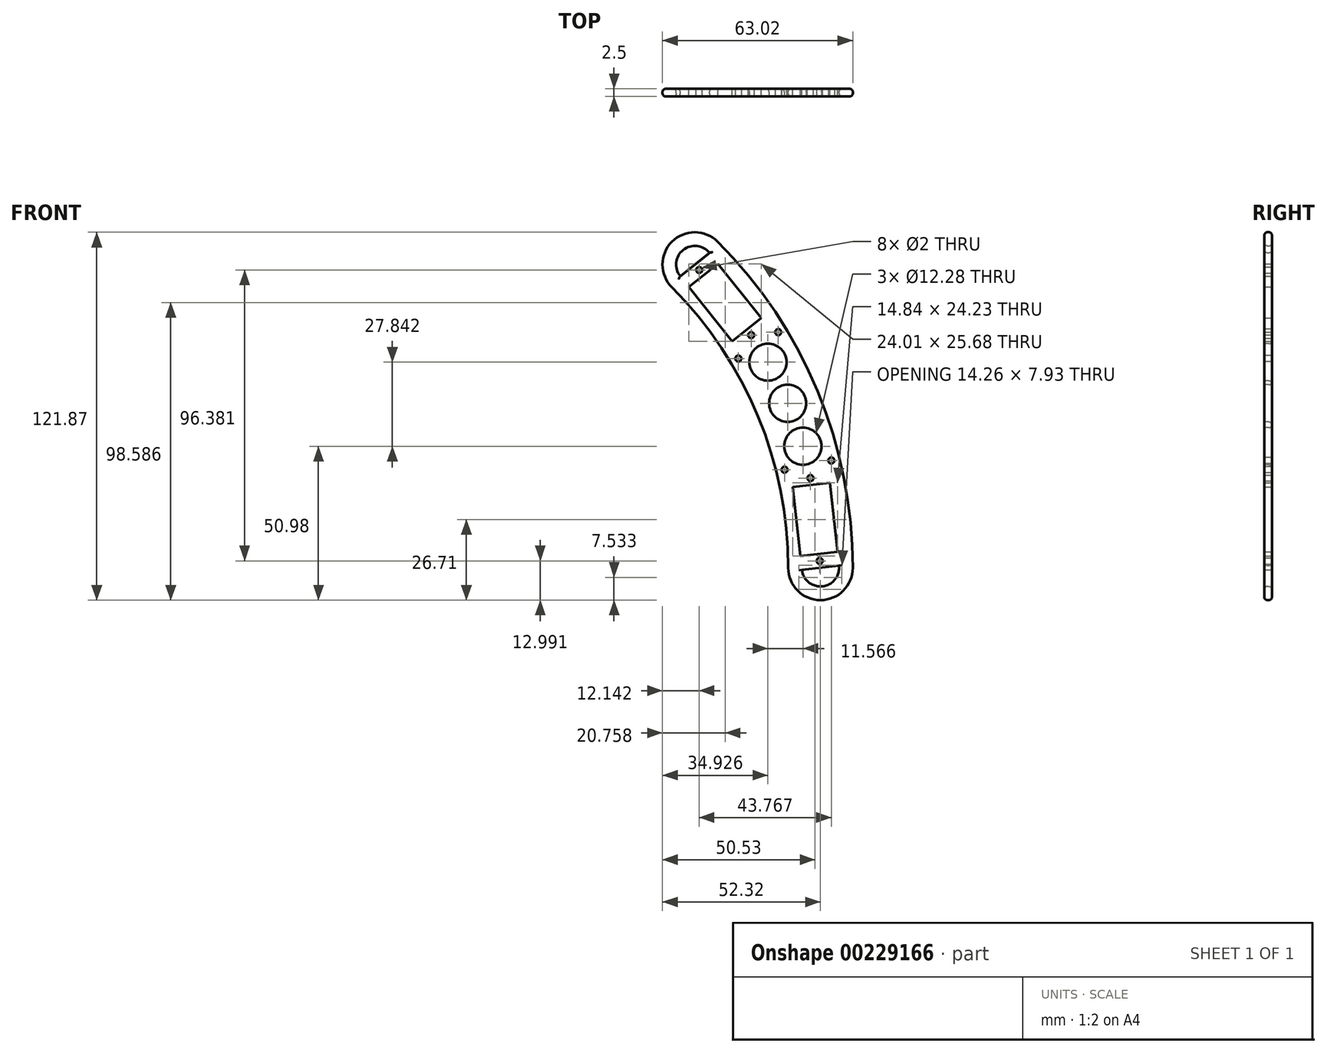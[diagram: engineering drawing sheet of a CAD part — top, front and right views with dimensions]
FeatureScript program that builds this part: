
annotation { "Feature Type Name" : "Feature", "Feature Type Description" : "" }
export const myFeature = defineFeature(function(context is Context, id is Id, definition is map)
    precondition{}
    {
        {
            var Q0;
            Q0=qCreatedBy(makeId("Front.planeOp"),FACE);
            var sketch = newSketch(context, id + "F0", { "sketchPlane" : qUnion([Q0])});
            skCircle(sketch, "E0", {"center": v(0, 0) * mm, "radius": 152.8 * mm});
            skCircle(sketch, "E1", {"center": v(0, 0) * mm, "radius": 131.4 * mm});
            skLineSegment(sketch, "E2", {"start": v(0, 0) * mm, "end": v(152.8, 0) * mm, "construction": true});
            skLineSegment(sketch, "E3", {"start": v(0, 0) * mm, "end": v(108.04, 108.04) * mm, "construction": true});
            skPoint(sketch, "E4", {"position": v(92.9, 92.9) * mm});
            skPoint(sketch, "E5", {"position": v(108.04, 108.04) * mm});
            skPoint(sketch, "E6", {"position": v(131.4, 0) * mm});
            skPoint(sketch, "E7", {"position": v(152.8, 0) * mm});
            skCircle(sketch, "E8", {"center": v(100.47, 100.47) * mm, "radius": 10.7 * mm});
            skCircle(sketch, "E9", {"center": v(142.1, 0) * mm, "radius": 10.7 * mm});
            skLineSegment(sketch, "E10", {"start": v(100.47, 100.47) * mm, "end": v(105.3, 104.33) * mm});
            skLineSegment(sketch, "E11", {"start": v(100.47, 100.47) * mm, "end": v(95.64, 96.62) * mm});
            skLineSegment(sketch, "E12", {"start": v(120.53, 75.25) * mm, "end": v(125.41, 79.16) * mm});
            skLineSegment(sketch, "E13", {"start": v(120.53, 75.25) * mm, "end": v(115.75, 71.44) * mm});
            skLineSegment(sketch, "E14", {"start": v(105.3, 104.33) * mm, "end": v(125.41, 79.16) * mm});
            skLineSegment(sketch, "E15", {"start": v(95.64, 96.62) * mm, "end": v(115.75, 71.44) * mm});
            skLineSegment(sketch, "E16", {"start": v(112.88, 75.04) * mm, "end": v(122.53, 82.76) * mm});
            skLineSegment(sketch, "E17", {"start": v(98.52, 93.01) * mm, "end": v(108.18, 100.73) * mm});
            skCircle(sketch, "E18", {"center": v(0, 0) * mm, "radius": 148.23 * mm, "construction": true});
            skCircle(sketch, "E19", {"center": v(0, 0) * mm, "radius": 135.95 * mm, "construction": true});
            skCircle(sketch, "E20", {"center": v(141.83, 2.3) * mm, "radius": 1 * mm});
            skLineSegment(sketch, "E21", {"start": v(122.53, 82.76) * mm, "end": v(115.75, 71.44) * mm, "construction": true});
            skLineSegment(sketch, "E22", {"start": v(112.88, 75.04) * mm, "end": v(125.41, 79.16) * mm, "construction": true});
            skCircle(sketch, "E23", {"center": v(101.91, 98.67) * mm, "radius": 1 * mm});
            skCircle(sketch, "E24", {"center": v(119.14, 77.1) * mm, "radius": 1 * mm});
            skCircle(sketch, "E25", {"center": v(107.2, 92.04) * mm, "radius": 6.18 * mm});
            skCircle(sketch, "E26", {"center": v(100.47, 100.47) * mm, "radius": 6.18 * mm});
            skCircle(sketch, "E27", {"center": v(142.1, 0) * mm, "radius": 6.17 * mm});
            skLineSegment(sketch, "E28", {"start": v(95.64, 96.62) * mm, "end": v(108.18, 100.73) * mm, "construction": true});
            skLineSegment(sketch, "E29", {"start": v(105.3, 104.33) * mm, "end": v(98.52, 93.01) * mm, "construction": true});
            skPoint(sketch, "E30", {"position": v(138.77, 29.73) * mm});
            skLineSegment(sketch, "E31", {"start": v(135.95, -0.69) * mm, "end": v(148.23, 0.69) * mm});
            skLineSegment(sketch, "E32", {"start": v(148.23, 0.69) * mm, "end": v(144.65, 32.7) * mm});
            skLineSegment(sketch, "E33", {"start": v(144.65, 32.7) * mm, "end": v(132.37, 31.33) * mm});
            skLineSegment(sketch, "E34", {"start": v(132.37, 31.33) * mm, "end": v(135.95, -0.69) * mm});
            skLineSegment(sketch, "E35", {"start": v(132.88, 26.75) * mm, "end": v(145.16, 28.13) * mm});
            skLineSegment(sketch, "E36", {"start": v(147.72, 5.27) * mm, "end": v(135.44, 3.9) * mm});
            skLineSegment(sketch, "E37", {"start": v(145.16, 28.13) * mm, "end": v(132.37, 31.33) * mm, "construction": true});
            skLineSegment(sketch, "E38", {"start": v(132.88, 26.75) * mm, "end": v(144.65, 32.7) * mm, "construction": true});
            skCircle(sketch, "E39", {"center": v(138.77, 29.73) * mm, "radius": 1 * mm});
            skLineSegment(sketch, "E40", {"start": v(147.72, 5.27) * mm, "end": v(135.95, -0.69) * mm, "construction": true});
            skLineSegment(sketch, "E41", {"start": v(148.23, 0.69) * mm, "end": v(135.44, 3.9) * mm, "construction": true});
            skCircle(sketch, "E42", {"center": v(140.9, 10.72) * mm, "radius": 6.18 * mm});
            skPoint(sketch, "E43", {"position": v(141.58, 4.58) * mm});
            skSolve(sketch);
        }
        {
            var Q0;
            {var subQ16=sQuery(id+"F0.wireOp",EDGE,"E13");Q0=makeQuery(id+"F0.imprint","IMPRINT",FACE,{"disambiguationData":[TD([[makeQuery(id+"F0.imprint","IMPRINT",EDGE,{"derivedFrom":subQ16}),1.0]])]});}
            var Q1;
            {var subQ14=sQuery(id+"F0.wireOp",EDGE,"E12");Q1=makeQuery(id+"F0.imprint","IMPRINT",FACE,{"disambiguationData":[TD([[makeQuery(id+"F0.imprint","IMPRINT",EDGE,{"derivedFrom":subQ14}),-1.0]])]});}
            var Q2;
            {var subQ3=sQuery(id+"F0.wireOp",EDGE,"oQQra7B9-EMDj-B2YQ-GpEd-beqhVWcHA2Qh");var subQ5=sQuery(id+"F0.wireOp",EDGE,"L7Lvz5JJ-y7Gk-G37b-dp0L-1B2kxOyyqlEU");var subQ9=makeQuery(id+"F0.imprint","INTERSECT",VERTEX,{"derivedFrom":[subQ3,subQ5]});Q2=makeQuery(id+"F0.imprint","IMPRINT",FACE,{"disambiguationData":[TD([[makeQuery(id+"F0.imprint","IMPRINT",EDGE,{"disambiguationData":[TD([[subQ9,-1.0]])],"derivedFrom":subQ3}),-1.0]])]});}
            var Q3;
            {var subQ3=sQuery(id+"F0.wireOp",EDGE,"oQQra7B9-EMDj-B2YQ-GpEd-beqhVWcHA2Qh");var subQ5=sQuery(id+"F0.wireOp",EDGE,"L7Lvz5JJ-y7Gk-G37b-dp0L-1B2kxOyyqlEU");var subQ9=makeQuery(id+"F0.imprint","INTERSECT",VERTEX,{"derivedFrom":[subQ3,subQ5]});Q3=makeQuery(id+"F0.imprint","IMPRINT",FACE,{"disambiguationData":[TD([[makeQuery(id+"F0.imprint","IMPRINT",EDGE,{"disambiguationData":[TD([[subQ9,-1.0]])],"derivedFrom":subQ3}),1.0]])]});}
            var Q4;
            {var subQ5=sQuery(id+"F0.wireOp",EDGE,"E9");var subQ8=makeQuery(id+"F0.imprint","INTERSECT",VERTEX,{"derivedFrom":[sQuery(id+"F0.wireOp",EDGE,"E1"),subQ5]});Q4=makeQuery(id+"F0.imprint","IMPRINT",FACE,{"disambiguationData":[TD([[makeQuery(id+"F0.imprint","IMPRINT",EDGE,{"disambiguationData":[TD([[subQ8,1.0]])],"derivedFrom":subQ5}),1.0]])]});}
            var Q5;
            {var subQ1=sQuery(id+"F0.wireOp",EDGE,"E9");var subQ5=makeQuery(id+"F0.imprint","INTERSECT",VERTEX,{"derivedFrom":[sQuery(id+"F0.wireOp",EDGE,"E0"),subQ1]});Q5=makeQuery(id+"F0.imprint","IMPRINT",FACE,{"disambiguationData":[TD([[makeQuery(id+"F0.imprint","IMPRINT",EDGE,{"disambiguationData":[TD([[subQ5,-1.0]])],"derivedFrom":subQ1}),1.0]])]});}
            var Q6;
            {var subQ1=sQuery(id+"F0.wireOp",EDGE,"pP7btSXe-vAWK-Rghq-c9eo-ooBtqokrkxCU");var subQ3=sQuery(id+"F0.wireOp",EDGE,"S4FxY1pI-YUIs-ADxV-D3kO-PCehrNdTsqgw");var subQ4=makeQuery(id+"F0.imprint","INTERSECT",VERTEX,{"derivedFrom":[subQ1,subQ3]});Q6=makeQuery(id+"F0.imprint","IMPRINT",FACE,{"disambiguationData":[TD([[makeQuery(id+"F0.imprint","IMPRINT",EDGE,{"disambiguationData":[TD([[subQ4,-1.0]])],"derivedFrom":subQ3}),-1.0]])]});}
            var Q7;
            {var subQ1=sQuery(id+"F0.wireOp",EDGE,"dObUoOk6-H3Xu-9Blf-IN91-eoC98K4MviYi");var subQ3=sQuery(id+"F0.wireOp",EDGE,"S4FxY1pI-YUIs-ADxV-D3kO-PCehrNdTsqgw");var subQ4=makeQuery(id+"F0.imprint","INTERSECT",VERTEX,{"derivedFrom":[subQ1,subQ3]});Q7=makeQuery(id+"F0.imprint","IMPRINT",FACE,{"disambiguationData":[TD([[makeQuery(id+"F0.imprint","IMPRINT",EDGE,{"disambiguationData":[TD([[subQ4,1.0]])],"derivedFrom":subQ3}),-1.0]])]});}
            var Q8;
            {var subQ4=sQuery(id+"F0.wireOp",EDGE,"E8");var subQ5=makeQuery(id+"F0.imprint","INTERSECT",VERTEX,{"derivedFrom":[sQuery(id+"F0.wireOp",EDGE,"E0"),subQ4]});Q8=makeQuery(id+"F0.imprint","IMPRINT",FACE,{"disambiguationData":[TD([[makeQuery(id+"F0.imprint","IMPRINT",EDGE,{"disambiguationData":[TD([[subQ5,-1.0]])],"derivedFrom":subQ4}),1.0]])]});}
            var Q9;
            {var subQ5=sQuery(id+"F0.wireOp",EDGE,"E8");var subQ9=makeQuery(id+"F0.imprint","INTERSECT",VERTEX,{"derivedFrom":[sQuery(id+"F0.wireOp",EDGE,"E1"),subQ5]});Q9=makeQuery(id+"F0.imprint","IMPRINT",FACE,{"disambiguationData":[TD([[makeQuery(id+"F0.imprint","IMPRINT",EDGE,{"disambiguationData":[TD([[subQ9,1.0]])],"derivedFrom":subQ5}),1.0]])]});}
            var Q10;
            {var subQ1=sQuery(id+"F0.wireOp",EDGE,"E15");var subQ3=sQuery(id+"F0.wireOp",EDGE,"E17");var subQ4=makeQuery(id+"F0.imprint","INTERSECT",VERTEX,{"derivedFrom":[subQ1,subQ3]});Q10=makeQuery(id+"F0.imprint","IMPRINT",FACE,{"disambiguationData":[TD([[makeQuery(id+"F0.imprint","IMPRINT",EDGE,{"disambiguationData":[TD([[subQ4,-1.0]])],"derivedFrom":subQ3}),1.0]])]});}
            var Q11;
            {var subQ4=sQuery(id+"F0.wireOp",EDGE,"E11");Q11=makeQuery(id+"F0.imprint","IMPRINT",FACE,{"disambiguationData":[TD([[makeQuery(id+"F0.imprint","IMPRINT",EDGE,{"derivedFrom":subQ4}),1.0]])]});}
            var Q12;
            {var subQ0=sQuery(id+"F0.wireOp",EDGE,"E10");Q12=makeQuery(id+"F0.imprint","IMPRINT",FACE,{"disambiguationData":[TD([[makeQuery(id+"F0.imprint","IMPRINT",EDGE,{"derivedFrom":subQ0}),-1.0]])]});}
            var Q13;
            {var subQ1=sQuery(id+"F0.wireOp",EDGE,"E14");var subQ3=sQuery(id+"F0.wireOp",EDGE,"E17");var subQ4=makeQuery(id+"F0.imprint","INTERSECT",VERTEX,{"derivedFrom":[subQ1,subQ3]});Q13=makeQuery(id+"F0.imprint","IMPRINT",FACE,{"disambiguationData":[TD([[makeQuery(id+"F0.imprint","IMPRINT",EDGE,{"disambiguationData":[TD([[subQ4,1.0]])],"derivedFrom":subQ3}),1.0]])]});}
            var Q14;
            {var subQ1=sQuery(id+"F0.wireOp",EDGE,"E13");Q14=makeQuery(id+"F0.imprint","IMPRINT",FACE,{"disambiguationData":[TD([[makeQuery(id+"F0.imprint","IMPRINT",EDGE,{"derivedFrom":subQ1}),-1.0]])]});}
            var Q15;
            {var subQ1=sQuery(id+"F0.wireOp",EDGE,"E12");Q15=makeQuery(id+"F0.imprint","IMPRINT",FACE,{"disambiguationData":[TD([[makeQuery(id+"F0.imprint","IMPRINT",EDGE,{"derivedFrom":subQ1}),1.0]])]});}
            var Q16;
            {var subQ0=sQuery(id+"F0.wireOp",EDGE,"OI4elRIE-cDK8-WTxH-k70q-1QsIJyjjSFf5");Q16=makeQuery(id+"F0.imprint","IMPRINT",FACE,{"disambiguationData":[TD([[makeQuery(id+"F0.imprint","IMPRINT",EDGE,{"derivedFrom":subQ0}),-1.0]])]});}
            var Q17;
            {var subQ5=sQuery(id+"F0.wireOp",EDGE,"jRu6URXB-eb1m-GeLn-RnXG-8x56v3XeeYK7");Q17=makeQuery(id+"F0.imprint","IMPRINT",FACE,{"disambiguationData":[TD([[makeQuery(id+"F0.imprint","IMPRINT",EDGE,{"derivedFrom":subQ5}),1.0]])]});}
            var Q18;
            Q18=makeQuery(id+"F0.imprint","IMPRINT",FACE,{"disambiguationData":[TD([[makeQuery(id+"F0.imprint","IMPRINT",EDGE,{"derivedFrom":sQuery(id+"F0.wireOp",EDGE,"E20")}),-1.0]])]});
            var Q19;
            {var subQ0=sQuery(id+"F0.wireOp",EDGE,"E36");var subQ1=sQuery(id+"F0.wireOp",EDGE,"E27");var subQ2=makeQuery(id+"F0.imprint","INTERSECT",VERTEX,{"disambiguationData":[OD(1.0)],"derivedFrom":[subQ1,subQ0]});Q19=makeQuery(id+"F0.imprint","IMPRINT",FACE,{"disambiguationData":[TD([[makeQuery(id+"F0.imprint","IMPRINT",EDGE,{"disambiguationData":[TD([[subQ2,-1.0]])],"derivedFrom":subQ1}),-1.0]])]});}
            var Q20;
            {var subQ0=sQuery(id+"F0.wireOp",EDGE,"E36");var subQ1=sQuery(id+"F0.wireOp",EDGE,"E27");var subQ2=makeQuery(id+"F0.imprint","INTERSECT",VERTEX,{"disambiguationData":[OD(0.0)],"derivedFrom":[subQ1,subQ0]});Q20=makeQuery(id+"F0.imprint","IMPRINT",FACE,{"disambiguationData":[TD([[makeQuery(id+"F0.imprint","IMPRINT",EDGE,{"disambiguationData":[TD([[subQ2,1.0]])],"derivedFrom":subQ1}),-1.0]])]});}
            var Q21;
            {var subQ2=sQuery(id+"F0.wireOp",EDGE,"E33");Q21=makeQuery(id+"F0.imprint","IMPRINT",FACE,{"disambiguationData":[TD([[makeQuery(id+"F0.imprint","IMPRINT",EDGE,{"derivedFrom":subQ2}),1.0]])]});}
            extrude(context, id + "F1", {"entities" : qUnion([Q0, Q1, Q2, Q3, Q4, Q5, Q6, Q7, Q8, Q9, Q10, Q11, Q12, Q13, Q14, Q15, Q16, Q17, Q18, Q19, Q20, Q21]), "depth" : 2.5 * mm});
        }
        {
            var Q0;
            Q0=makeQuery(id+"F1.opExtrude","CAP_FACE",FACE,{"disambiguationData":[OSD([sQuery(id+"F0.wireOp",EDGE,"E0"),sQuery(id+"F0.wireOp",EDGE,"E1"),sQuery(id+"F0.wireOp",EDGE,"E8"),sQuery(id+"F0.wireOp",EDGE,"E9"),sQuery(id+"F0.wireOp",EDGE,"jRu6URXB-eb1m-GeLn-RnXG-8x56v3XeeYK7"),sQuery(id+"F0.wireOp",EDGE,"SvjzzxK2-7mAt-kCR1-GuG7-fGwirkntV4HA"),sQuery(id+"F0.wireOp",EDGE,"dObUoOk6-H3Xu-9Blf-IN91-eoC98K4MviYi"),sQuery(id+"F0.wireOp",EDGE,"pP7btSXe-vAWK-Rghq-c9eo-ooBtqokrkxCU"),sQuery(id+"F0.wireOp",EDGE,"E10"),sQuery(id+"F0.wireOp",EDGE,"E11"),sQuery(id+"F0.wireOp",EDGE,"E14"),sQuery(id+"F0.wireOp",EDGE,"E15"),sQuery(id+"F0.wireOp",EDGE,"S4FxY1pI-YUIs-ADxV-D3kO-PCehrNdTsqgw"),sQuery(id+"F0.wireOp",EDGE,"L7Lvz5JJ-y7Gk-G37b-dp0L-1B2kxOyyqlEU"),sQuery(id+"F0.wireOp",EDGE,"E16"),sQuery(id+"F0.wireOp",EDGE,"E17"),sQuery(id+"F0.wireOp",EDGE,"E20"),sQuery(id+"F0.wireOp",EDGE,"xssTYC09-HPZV-zy9G-g6WS-DKxBsCUwhTFc"),sQuery(id+"F0.wireOp",EDGE,"E23"),sQuery(id+"F0.wireOp",EDGE,"E24"),sQuery(id+"F0.wireOp",EDGE,"E26"),sQuery(id+"F0.wireOp",EDGE,"E27")])],"isStart":false});
            var sketch = newSketch(context, id + "F2", { "sketchPlane" : qUnion([Q0])});
            skCircle(sketch, "E44", {"center": v(136.26, 40.28) * mm, "radius": 6.14 * mm});
            skCircle(sketch, "E45", {"center": v(124.7, 68.12) * mm, "radius": 6.14 * mm});
            skCircle(sketch, "E46", {"center": v(131.22, 54.5) * mm, "radius": 6.14 * mm});
            skCircle(sketch, "E47", {"center": v(0, 0) * mm, "radius": 142.1 * mm, "construction": true});
            skLineSegment(sketch, "E48", {"start": v(0, 0) * mm, "end": v(118, 79.14) * mm, "construction": true});
            skLineSegment(sketch, "E49", {"start": v(0, 0) * mm, "end": v(139.35, 27.76) * mm, "construction": true});
            skLineSegment(sketch, "E50", {"start": v(0, 0) * mm, "end": v(136.26, 40.28) * mm, "construction": true});
            skLineSegment(sketch, "E51", {"start": v(0, 0) * mm, "end": v(131.22, 54.5) * mm, "construction": true});
            skLineSegment(sketch, "E52", {"start": v(0, 0) * mm, "end": v(124.7, 68.12) * mm, "construction": true});
            skCircle(sketch, "E53", {"center": v(0, 0) * mm, "radius": 152.8 * mm, "construction": true});
            skCircle(sketch, "E54", {"center": v(0, 0) * mm, "radius": 131.4 * mm, "construction": true});
            skCircle(sketch, "E55", {"center": v(0, 0) * mm, "radius": 135.95 * mm, "construction": true});
            skCircle(sketch, "E56", {"center": v(0, 0) * mm, "radius": 148.23 * mm, "construction": true});
            skLineSegment(sketch, "E57", {"start": v(112.88, 75.04) * mm, "end": v(119.3, 65.18) * mm, "construction": true});
            skLineSegment(sketch, "E58", {"start": v(119.3, 65.18) * mm, "end": v(118, 79.14) * mm, "construction": true});
            skLineSegment(sketch, "E59", {"start": v(118, 79.14) * mm, "end": v(130.08, 71.07) * mm, "construction": true});
            skLineSegment(sketch, "E60", {"start": v(130.08, 71.07) * mm, "end": v(122.53, 82.76) * mm, "construction": true});
            skLineSegment(sketch, "E61", {"start": v(122.53, 82.76) * mm, "end": v(118, 79.14) * mm});
            skLineSegment(sketch, "E62", {"start": v(112.88, 75.04) * mm, "end": v(118, 79.14) * mm});
            skLineSegment(sketch, "E63", {"start": v(126.3, 76.91) * mm, "end": v(130.43, 79.57) * mm, "construction": true});
            skCircle(sketch, "E64", {"center": v(128.1, 78.07) * mm, "radius": 1 * mm});
            skLineSegment(sketch, "E65", {"start": v(130.37, 38.54) * mm, "end": v(132.76, 27) * mm});
            skLineSegment(sketch, "E66", {"start": v(145.04, 28.42) * mm, "end": v(142.22, 41.78) * mm});
            skLineSegment(sketch, "E67", {"start": v(131.57, 32.77) * mm, "end": v(127.45, 31.92) * mm});
            skLineSegment(sketch, "E68", {"start": v(143.63, 35.1) * mm, "end": v(148.46, 36.12) * mm});
            skCircle(sketch, "E69", {"center": v(130.18, 32.48) * mm, "radius": 1 * mm});
            skCircle(sketch, "E70", {"center": v(145.68, 35.54) * mm, "radius": 1 * mm});
            skLineSegment(sketch, "E71", {"start": v(116.1, 70.11) * mm, "end": v(112.55, 67.8) * mm, "construction": true});
            skCircle(sketch, "E72", {"center": v(114.87, 69.32) * mm, "radius": 1 * mm});
            skSolve(sketch);
        }
        {
            var Q0;
            Q0=makeQuery(id+"F2.imprint","IMPRINT",FACE,{"disambiguationData":[TD([[makeQuery(id+"F2.imprint","IMPRINT",EDGE,{"derivedFrom":sQuery(id+"F2.wireOp",EDGE,"E45")}),1.0]])]});
            var Q1;
            Q1=makeQuery(id+"F2.imprint","IMPRINT",FACE,{"disambiguationData":[TD([[makeQuery(id+"F2.imprint","IMPRINT",EDGE,{"derivedFrom":sQuery(id+"F2.wireOp",EDGE,"E46")}),1.0]])]});
            var Q2;
            Q2=makeQuery(id+"F2.imprint","IMPRINT",FACE,{"disambiguationData":[TD([[makeQuery(id+"F2.imprint","IMPRINT",EDGE,{"derivedFrom":sQuery(id+"F2.wireOp",EDGE,"E44")}),1.0]])]});
            var Q3;
            {var subQ0=sQuery(id+"F2.wireOp",EDGE,"E60");var subQ1=sQuery(id+"F2.wireOp",EDGE,"E45");var subQ2=makeQuery(id+"F2.imprint","INTERSECT",VERTEX,{"derivedFrom":[subQ1,subQ0]});Q3=makeQuery(id+"F2.imprint","IMPRINT",FACE,{"disambiguationData":[TD([[makeQuery(id+"F2.imprint","IMPRINT",EDGE,{"disambiguationData":[TD([[subQ2,-1.0]])],"derivedFrom":subQ1}),1.0]])]});}
            var Q4;
            {var subQ0=sQuery(id+"F2.wireOp",EDGE,"E58");var subQ1=sQuery(id+"F2.wireOp",EDGE,"E45");var subQ3=makeQuery(id+"F2.imprint","INTERSECT",VERTEX,{"derivedFrom":[subQ1,subQ0]});Q4=makeQuery(id+"F2.imprint","IMPRINT",FACE,{"disambiguationData":[TD([[makeQuery(id+"F2.imprint","IMPRINT",EDGE,{"disambiguationData":[TD([[subQ3,-1.0]])],"derivedFrom":subQ1}),1.0]])]});}
            var Q5;
            Q5=makeQuery(id+"F2.imprint","IMPRINT",FACE,{"disambiguationData":[TD([[makeQuery(id+"F2.imprint","IMPRINT",EDGE,{"derivedFrom":sQuery(id+"F2.wireOp",EDGE,"6Q9i7ZKX-M5Zn-dDvE-S5ua-DKoOSJd4rO0q")}),1.0]])]});
            var Q6;
            Q6=makeQuery(id+"F2.imprint","IMPRINT",FACE,{"disambiguationData":[TD([[makeQuery(id+"F2.imprint","IMPRINT",EDGE,{"derivedFrom":sQuery(id+"F2.wireOp",EDGE,"E64")}),1.0]])]});
            var Q7;
            Q7=makeQuery(id+"F2.imprint","IMPRINT",FACE,{"disambiguationData":[TD([[makeQuery(id+"F2.imprint","IMPRINT",EDGE,{"derivedFrom":sQuery(id+"F2.wireOp",EDGE,"E72")}),1.0]])]});
            var Q8;
            {var subQ0=sQuery(id+"F2.wireOp",EDGE,"E70");var subQ1=sQuery(id+"F2.wireOp",EDGE,"E68");var subQ2=makeQuery(id+"F2.imprint","INTERSECT",VERTEX,{"disambiguationData":[OD(0.0)],"derivedFrom":[subQ1,subQ0]});Q8=makeQuery(id+"F2.imprint","IMPRINT",FACE,{"disambiguationData":[TD([[makeQuery(id+"F2.imprint","IMPRINT",EDGE,{"disambiguationData":[TD([[subQ2,-1.0]])],"derivedFrom":subQ1}),1.0]])]});}
            var Q9;
            {var subQ0=sQuery(id+"F2.wireOp",EDGE,"E70");var subQ1=sQuery(id+"F2.wireOp",EDGE,"E68");var subQ2=makeQuery(id+"F2.imprint","INTERSECT",VERTEX,{"disambiguationData":[OD(0.0)],"derivedFrom":[subQ1,subQ0]});Q9=makeQuery(id+"F2.imprint","IMPRINT",FACE,{"disambiguationData":[TD([[makeQuery(id+"F2.imprint","IMPRINT",EDGE,{"disambiguationData":[TD([[subQ2,-1.0]])],"derivedFrom":subQ1}),-1.0]])]});}
            var Q10;
            {var subQ0=sQuery(id+"F2.wireOp",EDGE,"E69");var subQ1=sQuery(id+"F2.wireOp",EDGE,"E67");var subQ2=makeQuery(id+"F2.imprint","INTERSECT",VERTEX,{"disambiguationData":[OD(0.0)],"derivedFrom":[subQ1,subQ0]});Q10=makeQuery(id+"F2.imprint","IMPRINT",FACE,{"disambiguationData":[TD([[makeQuery(id+"F2.imprint","IMPRINT",EDGE,{"disambiguationData":[TD([[subQ2,-1.0]])],"derivedFrom":subQ1}),1.0]])]});}
            var Q11;
            {var subQ0=sQuery(id+"F2.wireOp",EDGE,"E69");var subQ1=sQuery(id+"F2.wireOp",EDGE,"E67");var subQ2=makeQuery(id+"F2.imprint","INTERSECT",VERTEX,{"disambiguationData":[OD(0.0)],"derivedFrom":[subQ1,subQ0]});Q11=makeQuery(id+"F2.imprint","IMPRINT",FACE,{"disambiguationData":[TD([[makeQuery(id+"F2.imprint","IMPRINT",EDGE,{"disambiguationData":[TD([[subQ2,-1.0]])],"derivedFrom":subQ1}),-1.0]])]});}
            extrude(context, id + "F3", {"entities" : qUnion([Q0, Q1, Q2, Q3, Q4, Q5, Q6, Q7, Q8, Q9, Q10, Q11]), "operationType" : NewBodyOperationType.REMOVE, "oppositeDirection" : true, "depth" : 25 * mm});
        }
        {
            var Q0;
            Q0=makeQuery(id+"F1.opExtrude","CAP_EDGE",EDGE,{"disambiguationData":[OSD([sQuery(id+"F0.wireOp",EDGE,"E27")])],"isStart":true});
            var Q1;
            Q1=makeQuery(id+"F1.opExtrude","CAP_EDGE",EDGE,{"disambiguationData":[OSD([sQuery(id+"F0.wireOp",EDGE,"E27")])],"isStart":false});
            var Q2;
            Q2=makeQuery(id+"F1.opExtrude","CAP_EDGE",EDGE,{"disambiguationData":[OSD([sQuery(id+"F0.wireOp",EDGE,"E9")])],"isStart":true});
            var Q3;
            Q3=makeQuery(id+"F1.opExtrude","CAP_EDGE",EDGE,{"disambiguationData":[OSD([sQuery(id+"F0.wireOp",EDGE,"E0")])],"isStart":false});
            var Q4;
            Q4=makeQuery(id+"F1.opExtrude","CAP_EDGE",EDGE,{"disambiguationData":[OSD([sQuery(id+"F0.wireOp",EDGE,"E26")])],"isStart":false});
            var Q5;
            Q5=makeQuery(id+"F1.opExtrude","CAP_EDGE",EDGE,{"disambiguationData":[OSD([sQuery(id+"F0.wireOp",EDGE,"E26")])],"isStart":true});
            var Q6;
            Q6=makeQuery(id+"F3.boolean.opBoolean","COPY",EDGE,{"derivedFrom":makeQuery(id+"F3.opExtrude","CAP_EDGE",EDGE,{"disambiguationData":[OSD([sQuery(id+"F2.wireOp",EDGE,"E45")])],"isStart":true})});
            var Q7;
            Q7=makeQuery(id+"F3.boolean.opBoolean","COPY",EDGE,{"derivedFrom":makeQuery(id+"F3.opExtrude","CAP_EDGE",EDGE,{"disambiguationData":[OSD([sQuery(id+"F2.wireOp",EDGE,"E46")])],"isStart":true})});
            var Q8;
            Q8=makeQuery(id+"F3.boolean.opBoolean","COPY",EDGE,{"derivedFrom":makeQuery(id+"F3.opExtrude","CAP_EDGE",EDGE,{"disambiguationData":[OSD([sQuery(id+"F2.wireOp",EDGE,"E44")])],"isStart":true})});
            var Q9;
            Q9=makeQuery(id+"F3.boolean.opBoolean","INTERSECT",EDGE,{"derivedFrom":[makeQuery(id+"F1.opExtrude","CAP_FACE",FACE,{"disambiguationData":[OSD([sQuery(id+"F0.wireOp",EDGE,"E0"),sQuery(id+"F0.wireOp",EDGE,"E1"),sQuery(id+"F0.wireOp",EDGE,"E8"),sQuery(id+"F0.wireOp",EDGE,"E9"),sQuery(id+"F0.wireOp",EDGE,"jRu6URXB-eb1m-GeLn-RnXG-8x56v3XeeYK7"),sQuery(id+"F0.wireOp",EDGE,"SvjzzxK2-7mAt-kCR1-GuG7-fGwirkntV4HA"),sQuery(id+"F0.wireOp",EDGE,"dObUoOk6-H3Xu-9Blf-IN91-eoC98K4MviYi"),sQuery(id+"F0.wireOp",EDGE,"pP7btSXe-vAWK-Rghq-c9eo-ooBtqokrkxCU"),sQuery(id+"F0.wireOp",EDGE,"E10"),sQuery(id+"F0.wireOp",EDGE,"E11"),sQuery(id+"F0.wireOp",EDGE,"E14"),sQuery(id+"F0.wireOp",EDGE,"E15"),sQuery(id+"F0.wireOp",EDGE,"S4FxY1pI-YUIs-ADxV-D3kO-PCehrNdTsqgw"),sQuery(id+"F0.wireOp",EDGE,"L7Lvz5JJ-y7Gk-G37b-dp0L-1B2kxOyyqlEU"),sQuery(id+"F0.wireOp",EDGE,"E16"),sQuery(id+"F0.wireOp",EDGE,"E17"),sQuery(id+"F0.wireOp",EDGE,"E20"),sQuery(id+"F0.wireOp",EDGE,"xssTYC09-HPZV-zy9G-g6WS-DKxBsCUwhTFc"),sQuery(id+"F0.wireOp",EDGE,"E23"),sQuery(id+"F0.wireOp",EDGE,"E24"),sQuery(id+"F0.wireOp",EDGE,"E26"),sQuery(id+"F0.wireOp",EDGE,"E27")])],"isStart":true}),makeQuery(id+"F3.opExtrude","SWEPT_FACE",FACE,{"disambiguationData":[OSD([sQuery(id+"F2.wireOp",EDGE,"E45")])]})]});
            var Q10;
            Q10=makeQuery(id+"F3.boolean.opBoolean","INTERSECT",EDGE,{"derivedFrom":[makeQuery(id+"F1.opExtrude","CAP_FACE",FACE,{"disambiguationData":[OSD([sQuery(id+"F0.wireOp",EDGE,"E0"),sQuery(id+"F0.wireOp",EDGE,"E1"),sQuery(id+"F0.wireOp",EDGE,"E8"),sQuery(id+"F0.wireOp",EDGE,"E9"),sQuery(id+"F0.wireOp",EDGE,"jRu6URXB-eb1m-GeLn-RnXG-8x56v3XeeYK7"),sQuery(id+"F0.wireOp",EDGE,"SvjzzxK2-7mAt-kCR1-GuG7-fGwirkntV4HA"),sQuery(id+"F0.wireOp",EDGE,"dObUoOk6-H3Xu-9Blf-IN91-eoC98K4MviYi"),sQuery(id+"F0.wireOp",EDGE,"pP7btSXe-vAWK-Rghq-c9eo-ooBtqokrkxCU"),sQuery(id+"F0.wireOp",EDGE,"E10"),sQuery(id+"F0.wireOp",EDGE,"E11"),sQuery(id+"F0.wireOp",EDGE,"E14"),sQuery(id+"F0.wireOp",EDGE,"E15"),sQuery(id+"F0.wireOp",EDGE,"S4FxY1pI-YUIs-ADxV-D3kO-PCehrNdTsqgw"),sQuery(id+"F0.wireOp",EDGE,"L7Lvz5JJ-y7Gk-G37b-dp0L-1B2kxOyyqlEU"),sQuery(id+"F0.wireOp",EDGE,"E16"),sQuery(id+"F0.wireOp",EDGE,"E17"),sQuery(id+"F0.wireOp",EDGE,"E20"),sQuery(id+"F0.wireOp",EDGE,"xssTYC09-HPZV-zy9G-g6WS-DKxBsCUwhTFc"),sQuery(id+"F0.wireOp",EDGE,"E23"),sQuery(id+"F0.wireOp",EDGE,"E24"),sQuery(id+"F0.wireOp",EDGE,"E26"),sQuery(id+"F0.wireOp",EDGE,"E27")])],"isStart":true}),makeQuery(id+"F3.opExtrude","SWEPT_FACE",FACE,{"disambiguationData":[OSD([sQuery(id+"F2.wireOp",EDGE,"E46")])]})]});
            var Q11;
            Q11=makeQuery(id+"F3.boolean.opBoolean","INTERSECT",EDGE,{"derivedFrom":[makeQuery(id+"F1.opExtrude","CAP_FACE",FACE,{"disambiguationData":[OSD([sQuery(id+"F0.wireOp",EDGE,"E0"),sQuery(id+"F0.wireOp",EDGE,"E1"),sQuery(id+"F0.wireOp",EDGE,"E8"),sQuery(id+"F0.wireOp",EDGE,"E9"),sQuery(id+"F0.wireOp",EDGE,"jRu6URXB-eb1m-GeLn-RnXG-8x56v3XeeYK7"),sQuery(id+"F0.wireOp",EDGE,"SvjzzxK2-7mAt-kCR1-GuG7-fGwirkntV4HA"),sQuery(id+"F0.wireOp",EDGE,"dObUoOk6-H3Xu-9Blf-IN91-eoC98K4MviYi"),sQuery(id+"F0.wireOp",EDGE,"pP7btSXe-vAWK-Rghq-c9eo-ooBtqokrkxCU"),sQuery(id+"F0.wireOp",EDGE,"E10"),sQuery(id+"F0.wireOp",EDGE,"E11"),sQuery(id+"F0.wireOp",EDGE,"E14"),sQuery(id+"F0.wireOp",EDGE,"E15"),sQuery(id+"F0.wireOp",EDGE,"S4FxY1pI-YUIs-ADxV-D3kO-PCehrNdTsqgw"),sQuery(id+"F0.wireOp",EDGE,"L7Lvz5JJ-y7Gk-G37b-dp0L-1B2kxOyyqlEU"),sQuery(id+"F0.wireOp",EDGE,"E16"),sQuery(id+"F0.wireOp",EDGE,"E17"),sQuery(id+"F0.wireOp",EDGE,"E20"),sQuery(id+"F0.wireOp",EDGE,"xssTYC09-HPZV-zy9G-g6WS-DKxBsCUwhTFc"),sQuery(id+"F0.wireOp",EDGE,"E23"),sQuery(id+"F0.wireOp",EDGE,"E24"),sQuery(id+"F0.wireOp",EDGE,"E26"),sQuery(id+"F0.wireOp",EDGE,"E27")])],"isStart":true}),makeQuery(id+"F3.opExtrude","SWEPT_FACE",FACE,{"disambiguationData":[OSD([sQuery(id+"F2.wireOp",EDGE,"E44")])]})]});
            fillet(context, id + "F4", {"entities" : qUnion([Q0, Q1, Q2, Q3, Q4, Q5, Q6, Q7, Q8, Q9, Q10, Q11]), "radius" : 1 * mm, "tangentPropagation" : true, "allowEdgeOverflow" : false});
        }
        {
            var Q0;
            Q0=makeQuery(id+"F1.opExtrude","CAP_EDGE",EDGE,{"disambiguationData":[OSD([sQuery(id+"F0.wireOp",EDGE,"E10"),sQuery(id+"F0.wireOp",EDGE,"E11")])],"isStart":false});
            var Q1;
            Q1=makeQuery(id+"F1.opExtrude","CAP_EDGE",EDGE,{"disambiguationData":[OSD([sQuery(id+"F0.wireOp",EDGE,"E10"),sQuery(id+"F0.wireOp",EDGE,"E11")])],"isStart":true});
            var Q2;
            Q2=makeQuery(id+"F1.opExtrude","CAP_EDGE",EDGE,{"disambiguationData":[OSD([sQuery(id+"F0.wireOp",EDGE,"jRu6URXB-eb1m-GeLn-RnXG-8x56v3XeeYK7"),sQuery(id+"F0.wireOp",EDGE,"SvjzzxK2-7mAt-kCR1-GuG7-fGwirkntV4HA")])],"isStart":true});
            var Q3;
            Q3=makeQuery(id+"F1.opExtrude","CAP_EDGE",EDGE,{"disambiguationData":[OSD([sQuery(id+"F0.wireOp",EDGE,"jRu6URXB-eb1m-GeLn-RnXG-8x56v3XeeYK7"),sQuery(id+"F0.wireOp",EDGE,"SvjzzxK2-7mAt-kCR1-GuG7-fGwirkntV4HA")])],"isStart":false});
            fillet(context, id + "F5", {"entities" : qUnion([Q0, Q1, Q2, Q3]), "radius" : 0.5 * mm, "tangentPropagation" : true, "allowEdgeOverflow" : false});
        }
    });
